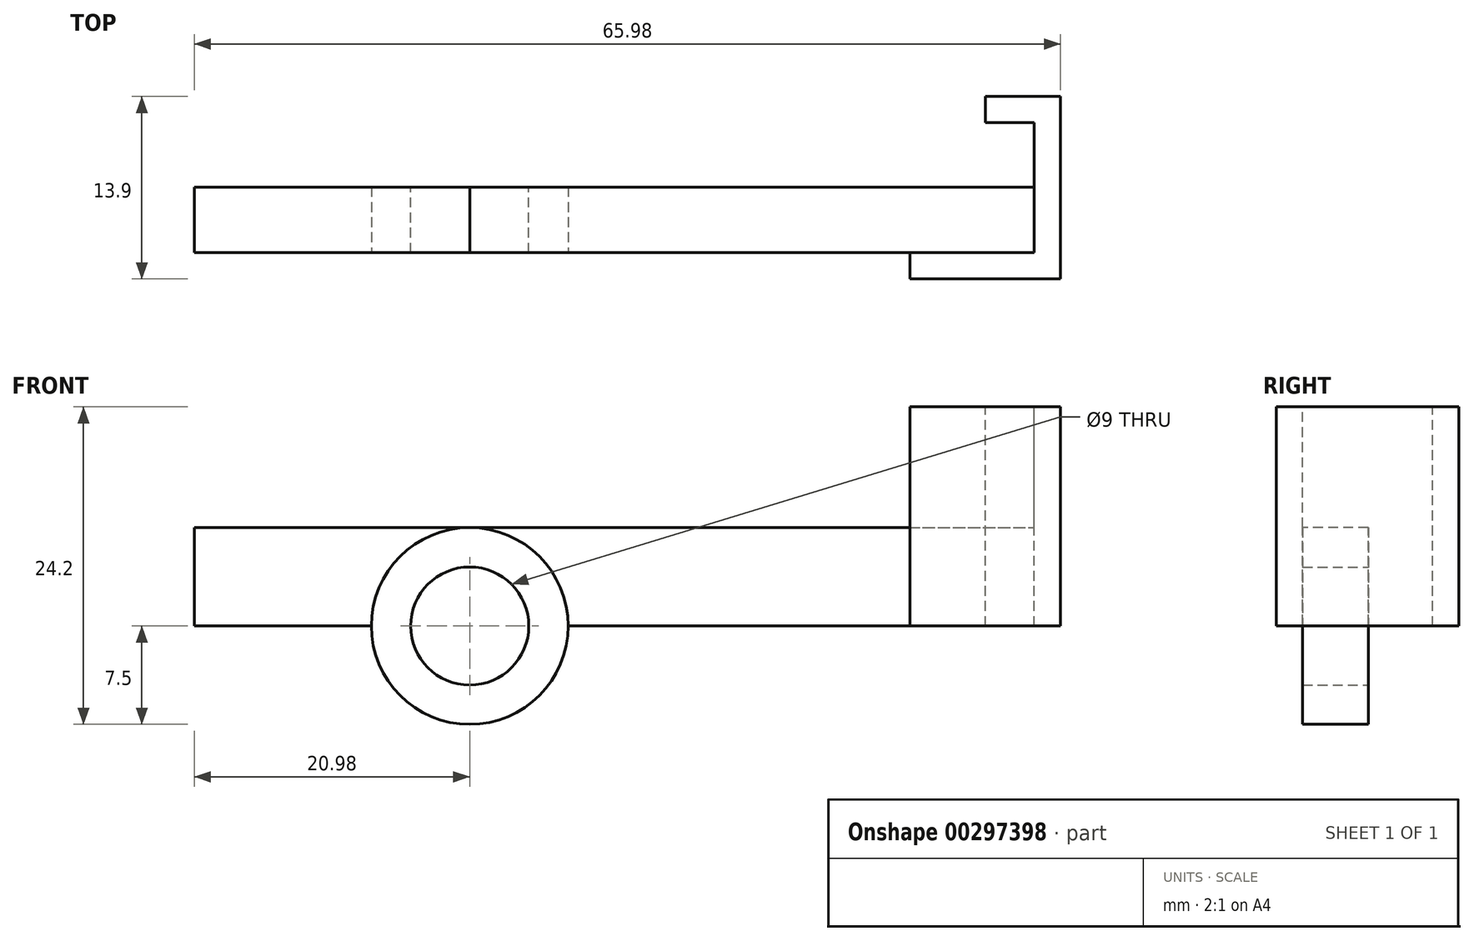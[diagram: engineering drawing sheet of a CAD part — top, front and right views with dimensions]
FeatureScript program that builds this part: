
annotation { "Feature Type Name" : "Feature", "Feature Type Description" : "" }
export const myFeature = defineFeature(function(context is Context, id is Id, definition is map)
    precondition{}
    {
        {
            var Q0;
            Q0=qCreatedBy(makeId("Front.planeOp"),FACE);
            var sketch = newSketch(context, id + "F0", { "sketchPlane" : qUnion([Q0])});
            skCircle(sketch, "E0", {"center": v(0, 0) * mm, "radius": 4.5 * mm});
            skCircle(sketch, "E1.0", {"center": v(0, 0) * mm, "radius": 7.5 * mm});
            skSolve(sketch);
        }
        {
            var Q0;
            Q0=makeQuery(id+"F0.imprint","IMPRINT",FACE,{"disambiguationData":[TD([[makeQuery(id+"F0.imprint","IMPRINT",EDGE,{"derivedFrom":sQuery(id+"F0.wireOp",EDGE,"E0")}),-1.0]])]});
            extrude(context, id + "F1", {"entities" : qUnion([Q0]), "depth" : 5 * mm});
        }
        {
            var Q0;
            Q0=makeQuery(id+"F1.opExtrude","CAP_FACE",FACE,{"disambiguationData":[OSD([sQuery(id+"F0.wireOp",EDGE,"E0"),sQuery(id+"F0.wireOp",EDGE,"E1.0")])],"isStart":false});
            var sketch = newSketch(context, id + "F2", { "sketchPlane" : qUnion([Q0])});
            skLineSegment(sketch, "E2.bottom", {"start": v(0, 0) * mm, "end": v(43, 0) * mm});
            skLineSegment(sketch, "E2.top", {"start": v(0, 7.5) * mm, "end": v(43, 7.5) * mm});
            skLineSegment(sketch, "E2.left", {"start": v(0, 0) * mm, "end": v(0, 7.5) * mm});
            skLineSegment(sketch, "E2.right", {"start": v(43, 0) * mm, "end": v(43, 7.5) * mm});
            skLineSegment(sketch, "E3.bottom", {"start": v(0, 7.5) * mm, "end": v(-20.98, 7.5) * mm});
            skLineSegment(sketch, "E3.top", {"start": v(0, 0) * mm, "end": v(-20.98, 0) * mm});
            skLineSegment(sketch, "E3.left", {"start": v(0, 7.5) * mm, "end": v(0, 0) * mm});
            skLineSegment(sketch, "E3.right", {"start": v(-20.98, 7.5) * mm, "end": v(-20.98, 0) * mm});
            skSolve(sketch);
        }
        {
            var Q0;
            {var subQ0=sQuery(id+"F2.wireOp",EDGE,"E3.bottom");Q0=makeQuery(id+"F2.imprint","IMPRINT",FACE,{"disambiguationData":[TD([[makeQuery(id+"F2.imprint","IMPRINT",EDGE,{"derivedFrom":subQ0}),1.0]])]});}
            var Q1;
            {var subQ4=sQuery(id+"F2.wireOp",EDGE,"E2.top");Q1=makeQuery(id+"F2.imprint","IMPRINT",FACE,{"disambiguationData":[TD([[makeQuery(id+"F2.imprint","IMPRINT",EDGE,{"derivedFrom":subQ4}),-1.0]])]});}
            extrude(context, id + "F3", {"entities" : qUnion([Q0, Q1]), "oppositeDirection" : true, "depth" : 5 * mm});
        }
        {
            var Q0;
            Q0=makeQuery(id+"F3.opExtrude","SWEPT_FACE",FACE,{"disambiguationData":[OSD([sQuery(id+"F2.wireOp",EDGE,"E2.right")])]});
            var sketch = newSketch(context, id + "F4", { "sketchPlane" : qUnion([Q0])});
            skLineSegment(sketch, "E4.bottom", {"start": v(-5, 0) * mm, "end": v(4.9, 0) * mm});
            skLineSegment(sketch, "E4.top", {"start": v(-5, 16.7) * mm, "end": v(4.9, 16.7) * mm});
            skLineSegment(sketch, "E4.left", {"start": v(-5, 0) * mm, "end": v(-5, 16.7) * mm});
            skLineSegment(sketch, "E4.right", {"start": v(4.9, 0) * mm, "end": v(4.9, 16.7) * mm});
            skSolve(sketch);
        }
        {
            var Q0;
            {var subQ3=sQuery(id+"F4.wireOp",EDGE,"E4.top");Q0=makeQuery(id+"F4.imprint","IMPRINT",FACE,{"disambiguationData":[TD([[makeQuery(id+"F4.imprint","IMPRINT",EDGE,{"derivedFrom":subQ3}),-1.0]])]});}
            var Q1;
            {var subQ3=sQuery(id+"F2.wireOp",EDGE,"E2.right");var subQ4=makeQuery(id+"F3.opExtrude","CAP_EDGE",EDGE,{"disambiguationData":[OSD([subQ3])],"isStart":false});Q1=makeQuery(id+"F4.imprint","IMPRINT",FACE,{"disambiguationData":[TD([[makeQuery(id+"F4.imprint","IMPRINT",EDGE,{"derivedFrom":subQ4}),1.0]])]});}
            extrude(context, id + "F5", {"entities" : qUnion([Q0, Q1]), "operationType" : NewBodyOperationType.ADD, "depth" : 2 * mm});
        }
        {
            var Q0;
            Q0=makeQuery(id+"F5.opExtrude","SWEPT_FACE",FACE,{"disambiguationData":[OSD([sQuery(id+"F4.wireOp",EDGE,"E4.right")])]});
            var sketch = newSketch(context, id + "F6", { "sketchPlane" : qUnion([Q0])});
            skLineSegment(sketch, "E5.bottom", {"start": v(-45, 0) * mm, "end": v(-39.27, 0) * mm});
            skLineSegment(sketch, "E5.top", {"start": v(-45, 16.7) * mm, "end": v(-39.27, 16.7) * mm});
            skLineSegment(sketch, "E5.left", {"start": v(-45, 0) * mm, "end": v(-45, 16.7) * mm});
            skLineSegment(sketch, "E5.right", {"start": v(-39.27, 0) * mm, "end": v(-39.27, 16.7) * mm});
            skSolve(sketch);
        }
        {
            var Q0;
            {var subQ2=sQuery(id+"F6.wireOp",EDGE,"E5.right");Q0=makeQuery(id+"F6.imprint","IMPRINT",FACE,{"disambiguationData":[TD([[makeQuery(id+"F6.imprint","IMPRINT",EDGE,{"derivedFrom":subQ2}),1.0]])]});}
            var Q1;
            {var subQ2=sQuery(id+"F6.wireOp",EDGE,"E5.left");Q1=makeQuery(id+"F6.imprint","IMPRINT",FACE,{"disambiguationData":[TD([[makeQuery(id+"F6.imprint","IMPRINT",EDGE,{"derivedFrom":subQ2}),-1.0]])]});}
            extrude(context, id + "F7", {"entities" : qUnion([Q0, Q1]), "operationType" : NewBodyOperationType.ADD, "depth" : 2 * mm});
        }
        {
            var Q0;
            Q0=makeQuery(id+"F5.boolean.opBoolean","MERGE",FACE,{"derivedFrom":[makeQuery(id+"F3.opExtrude","CAP_FACE",FACE,{"disambiguationData":[OSD([sQuery(id+"F0.wireOp",EDGE,"E1.0"),sQuery(id+"F2.wireOp",EDGE,"E2.bottom"),sQuery(id+"F2.wireOp",EDGE,"E2.top"),sQuery(id+"F2.wireOp",EDGE,"E2.right")])],"isStart":true}),makeQuery(id+"F5.opExtrude","SWEPT_FACE",FACE,{"disambiguationData":[OSD([sQuery(id+"F4.wireOp",EDGE,"E4.left")])]})]});
            var sketch = newSketch(context, id + "F8", { "sketchPlane" : qUnion([Q0])});
            skLineSegment(sketch, "E6.bottom", {"start": v(45, 0) * mm, "end": v(33.55, 0) * mm});
            skLineSegment(sketch, "E6.top", {"start": v(45, 16.7) * mm, "end": v(33.55, 16.7) * mm});
            skLineSegment(sketch, "E6.left", {"start": v(45, 0) * mm, "end": v(45, 16.7) * mm});
            skLineSegment(sketch, "E6.right", {"start": v(33.55, 0) * mm, "end": v(33.55, 16.7) * mm});
            skSolve(sketch);
        }
        {
            var Q0;
            {var subQ1=makeQuery(id+"F5.opExtrude","CAP_EDGE",EDGE,{"disambiguationData":[OSD([sQuery(id+"F4.wireOp",EDGE,"E4.left")])],"isStart":true});Q0=makeQuery(id+"F8.imprint","IMPRINT",FACE,{"disambiguationData":[TD([[makeQuery(id+"F8.imprint","IMPRINT",EDGE,{"derivedFrom":subQ1}),1.0]])]});}
            var Q1;
            {var subQ1=sQuery(id+"F8.wireOp",EDGE,"E6.bottom");Q1=makeQuery(id+"F8.imprint","IMPRINT",FACE,{"disambiguationData":[TD([[makeQuery(id+"F8.imprint","IMPRINT",EDGE,{"derivedFrom":subQ1}),1.0]])]});}
            extrude(context, id + "F9", {"entities" : qUnion([Q0, Q1]), "operationType" : NewBodyOperationType.ADD, "depth" : 2 * mm});
        }
    });
